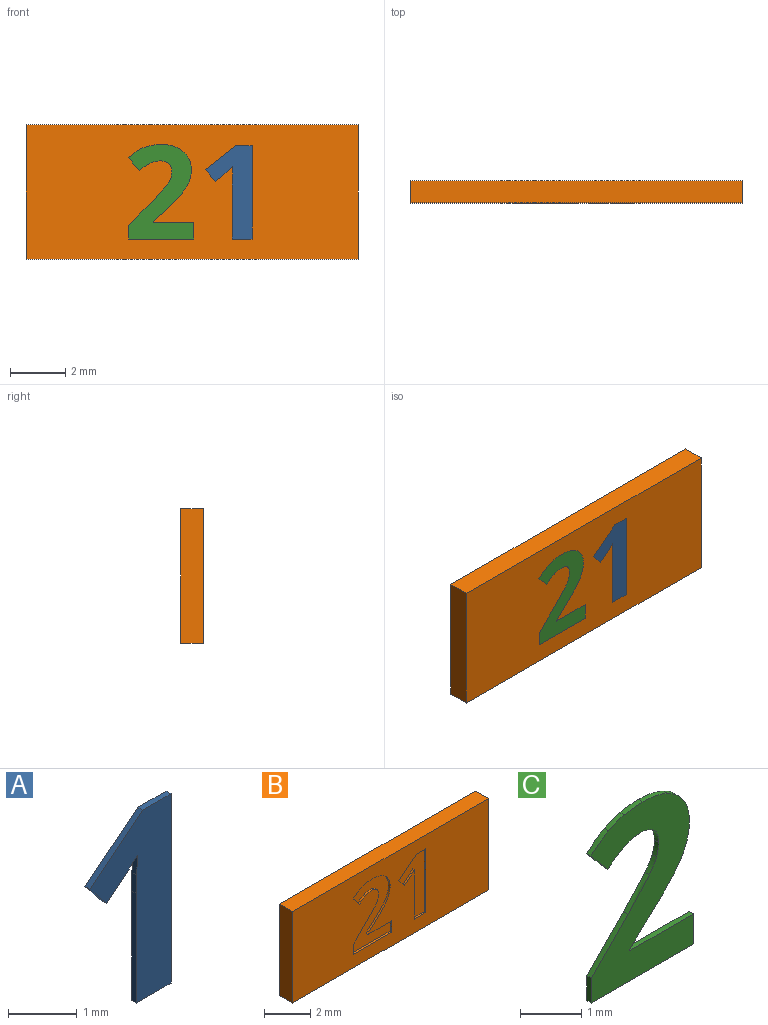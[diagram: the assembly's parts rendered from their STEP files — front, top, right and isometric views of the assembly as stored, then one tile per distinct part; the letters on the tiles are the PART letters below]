
ASSEMBLY  parts=3 mates=2
PART A: 12 faces, bbox 1.7x0.1x3.4 mm
  f0: plane 3.37x1.67mm, normal (0,-1,0), area 2.9mm2, adj f1,f2,f3,f4,f5,f6,f7,f9
  f1: plane 0.59x0.1mm, normal (0,0,1), area 0.1mm2, adj f0,f2,f8,f10
  f2: plane 1.09x0.86mm, normal (-0.62,0,0.78), area 0.1mm2, adj f0,f1,f3,f8
  f3: plane 0.43x0.34mm, normal (-0.78,0,-0.63), area 0.1mm2, adj f0,f2,f4,f8
  f4: plane 0.39x0.31mm, normal (0.63,0,-0.78), area 0mm2, adj f0,f3,f5,f8
  f5: extruded ~0.25x0.23mm, area 0mm2, adj f0,f4,f6,f8
  f6: plane 0.35x0.1mm, normal (-1,0,0.03), area 0mm2, adj f0,f5,f7,f8
  f7: plane 0.32x0.1mm, normal (-1,0,0.02), area 0mm2, adj f0,f6,f8,f9
  f8: plane 3.37x1.67mm, normal (0,1,0), area 2.9mm2, adj f1,f2,f3,f4,f5,f6,f7,f9
  f9: plane 1.95x0.1mm, normal (-1,0,0), area 0.2mm2, adj f0,f7,f8,f11
  f10: plane 3.37x0.1mm, normal (1,0,0), area 0.3mm2, adj f0,f1,f8,f11
  f11: plane 0.71x0.1mm, normal (0,0,-1), area 0.1mm2, adj f0,f8,f9,f10
PART B: 42 faces, bbox 12x0.8x4.9 mm
  f0: plane 12x4.85mm, normal (0,-1,0), area 51mm2, adj f1,f2,f3,f4,f6,f7,f8,f9
  f1: plane 4.85x0.8mm, normal (1,0,0), area 3.9mm2, adj f0,f2,f4,f5
  f2: plane 12x0.8mm, normal (0,0,1), area 9.6mm2, adj f0,f1,f3,f5
  f3: plane 4.85x0.8mm, normal (-1,0,0), area 3.9mm2, adj f0,f2,f4,f5
  f4: plane 12x0.8mm, normal (0,0,-1), area 9.6mm2, adj f0,f1,f3,f5
  f5: plane 12x4.85mm, normal (0,1,0), area 58.2mm2, adj f1,f2,f3,f4
  f6: plane 3.37x0.1mm, normal (-1,0,0), area 0.3mm2, adj f0,f7,f15,f16
  f7: plane 0.59x0.1mm, normal (0,0,-1), area 0.1mm2, adj f0,f6,f8,f16
  f8: plane 1.09x0.86mm, normal (0.62,0,-0.78), area 0.1mm2, adj f0,f7,f9,f16
  f9: plane 0.43x0.34mm, normal (0.78,0,0.63), area 0.1mm2, adj f0,f8,f10,f16
  f10: plane 0.39x0.31mm, normal (-0.63,0,0.78), area 0mm2, adj f0,f9,f11,f16
  f11: extruded ~0.25x0.23mm, area 0mm2, adj f0,f10,f12,f16
  f12: plane 0.35x0.1mm, normal (1,0,-0.03), area 0mm2, adj f0,f11,f13,f16
  f13: plane 0.32x0.1mm, normal (1,0,-0.02), area 0mm2, adj f0,f12,f14,f16
  f14: plane 1.95x0.1mm, normal (1,0,0), area 0.2mm2, adj f0,f13,f15,f16
  f15: plane 0.71x0.1mm, normal (0,0,1), area 0.1mm2, adj f0,f6,f14,f16
  f16: plane 3.37x1.67mm, normal (0,-1,0), area 2.9mm2, adj f6,f7,f8,f9,f10,f11,f12,f13
  f17: plane 0.6x0.1mm, normal (-1,0,0), area 0.1mm2, adj f0,f18,f40,f41
  f18: plane 1.47x0.1mm, normal (0,0,-1), area 0.1mm2, adj f0,f17,f19,f41
  f19: plane 0.1x0.03mm, normal (-1,0,0), area 0mm2, adj f0,f18,f20,f41
  f20: plane 0.43x0.41mm, normal (-0.69,0,0.73), area 0.1mm2, adj f0,f19,f21,f41
  f21: extruded ~0.61x0.61mm, area 0.1mm2, adj f0,f20,f22,f41
  f22: extruded ~0.42x0.25mm, area 0mm2, adj f0,f21,f23,f41
  f23: extruded ~0.44x0.1mm, area 0mm2, adj f0,f22,f24,f41
  f24: extruded ~0.48x0.13mm, area 0.1mm2, adj f0,f23,f25,f41
  f25: extruded ~0.38x0.32mm, area 0.1mm2, adj f0,f24,f26,f41
  f26: extruded ~0.56x0.12mm, area 0.1mm2, adj f0,f25,f27,f41
  f27: extruded ~0.43x0.1mm, area 0mm2, adj f0,f26,f28,f41
  f28: extruded ~0.36x0.13mm, area 0mm2, adj f0,f27,f29,f41
  f29: extruded ~0.41x0.3mm, area 0.1mm2, adj f0,f28,f30,f41
  f30: plane 0.46x0.39mm, normal (0.76,0,0.65), area 0.1mm2, adj f0,f29,f31,f41
  f31: extruded ~0.39x0.26mm, area 0mm2, adj f0,f30,f32,f41
  f32: extruded ~0.38x0.1mm, area 0mm2, adj f0,f31,f33,f41
  f33: extruded ~0.3x0.1mm, area 0mm2, adj f0,f32,f34,f41
  f34: extruded ~0.3x0.11mm, area 0mm2, adj f0,f33,f35,f41
  f35: extruded ~0.26x0.1mm, area 0mm2, adj f0,f34,f36,f41
  f36: extruded ~0.28x0.17mm, area 0mm2, adj f0,f35,f37,f41
  f37: extruded ~0.53x0.49mm, area 0.1mm2, adj f0,f36,f38,f41
  f38: plane 0.86x0.85mm, normal (0.71,0,-0.7), area 0.1mm2, adj f0,f37,f39,f41
  f39: plane 0.5x0.1mm, normal (1,0,0), area 0mm2, adj f0,f38,f40,f41
  f40: plane 2.36x0.1mm, normal (0,0,1), area 0.2mm2, adj f0,f17,f39,f41
  f41: plane 3.42x2.37mm, normal (0,-1,0), area 4.2mm2, adj f17,f18,f19,f20,f21,f22,f23,f24
PART C: 26 faces, bbox 2.4x0.1x3.4 mm
  f0: plane 3.42x2.37mm, normal (0,-1,0), area 4.2mm2, adj f1,f2,f3,f4,f5,f6,f7,f8
  f1: plane 1.47x0.1mm, normal (0,0,1), area 0.1mm2, adj f0,f2,f22,f24
  f2: plane 0.1x0.03mm, normal (1,0,0), area 0mm2, adj f0,f1,f3,f22
  f3: plane 0.43x0.41mm, normal (0.69,0,-0.73), area 0.1mm2, adj f0,f2,f4,f22
  f4: extruded ~0.61x0.61mm, area 0.1mm2, adj f0,f3,f5,f22
  f5: extruded ~0.42x0.25mm, area 0mm2, adj f0,f4,f6,f22
  f6: extruded ~0.44x0.1mm, area 0mm2, adj f0,f5,f7,f22
  f7: extruded ~0.48x0.13mm, area 0.1mm2, adj f0,f6,f8,f22
  f8: extruded ~0.38x0.32mm, area 0.1mm2, adj f0,f7,f9,f22
  f9: extruded ~0.56x0.12mm, area 0.1mm2, adj f0,f8,f10,f22
  f10: extruded ~0.43x0.1mm, area 0mm2, adj f0,f9,f11,f22
  f11: extruded ~0.36x0.13mm, area 0mm2, adj f0,f10,f12,f22
  f12: extruded ~0.41x0.3mm, area 0.1mm2, adj f0,f11,f13,f22
  f13: plane 0.46x0.39mm, normal (-0.76,0,-0.65), area 0.1mm2, adj f0,f12,f14,f22
  f14: extruded ~0.39x0.26mm, area 0mm2, adj f0,f13,f15,f22
  f15: extruded ~0.38x0.1mm, area 0mm2, adj f0,f14,f16,f22
  f16: extruded ~0.3x0.1mm, area 0mm2, adj f0,f15,f17,f22
  f17: extruded ~0.3x0.11mm, area 0mm2, adj f0,f16,f18,f22
  f18: extruded ~0.26x0.1mm, area 0mm2, adj f0,f17,f19,f22
  f19: extruded ~0.28x0.17mm, area 0mm2, adj f0,f18,f20,f22
  f20: extruded ~0.53x0.49mm, area 0.1mm2, adj f0,f19,f21,f22
  f21: plane 0.86x0.85mm, normal (-0.71,0,0.7), area 0.1mm2, adj f0,f20,f22,f23
  f22: plane 3.42x2.37mm, normal (0,1,0), area 4.2mm2, adj f1,f2,f3,f4,f5,f6,f7,f8
  f23: plane 0.5x0.1mm, normal (-1,0,0), area 0mm2, adj f0,f21,f22,f25
  f24: plane 0.6x0.1mm, normal (1,0,0), area 0.1mm2, adj f0,f1,f22,f25
  f25: plane 2.36x0.1mm, normal (0,0,-1), area 0.2mm2, adj f0,f22,f23,f24
PLACE A t=(-0.21,0.39,-0.03)mm
PLACE B t=(0.01,0.39,-0.03)mm
PLACE C t=(-2.61,0.39,-0.03)mm
MATE fastened A.f0 <-> B.f0  axis (0,-1,0) through (1.47,-0.41,-1.73)mm
MATE fastened C.f0 <-> B.f0  axis (0,-1,0) through (-2.28,-0.41,-1.73)mm
